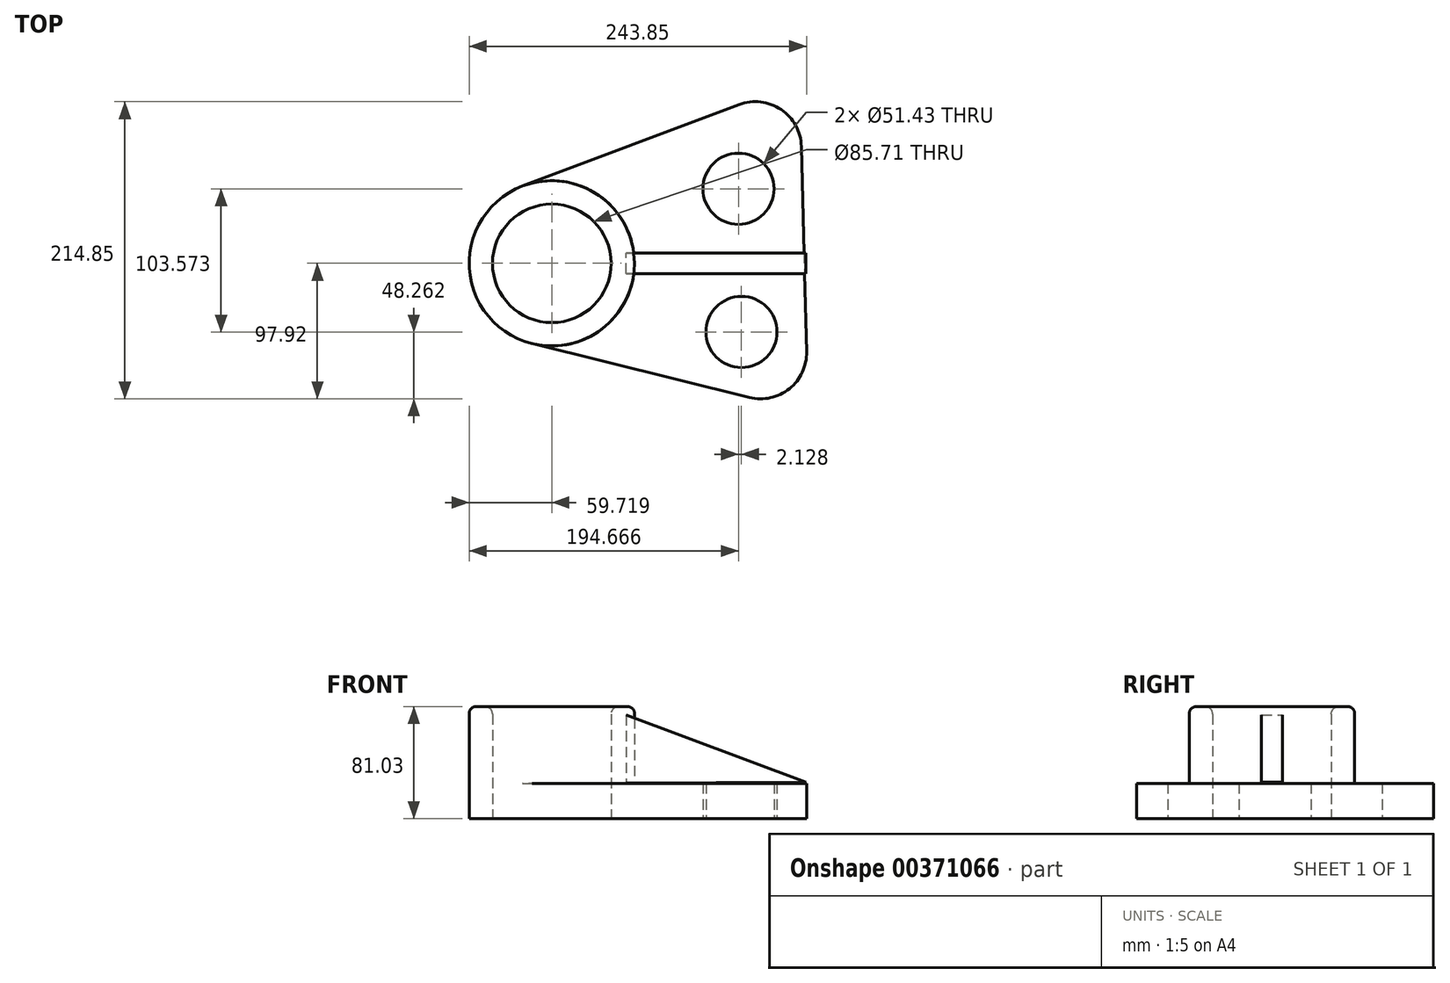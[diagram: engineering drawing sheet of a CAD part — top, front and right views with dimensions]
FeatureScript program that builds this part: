
annotation { "Feature Type Name" : "Feature", "Feature Type Description" : "" }
export const myFeature = defineFeature(function(context is Context, id is Id, definition is map)
    precondition{}
    {
        {
            var Q0;
            Q0=qCreatedBy(makeId("Top.planeOp"),FACE);
            var sketch = newSketch(context, id + "F0", { "sketchPlane" : qUnion([Q0])});
            skCircle(sketch, "E0", {"center": v(-65.07, 0) * mm, "radius": 59.72 * mm});
            skLineSegment(sketch, "E1", {"start": v(-79.44, -57.97) * mm, "end": v(120.16, -107.43) * mm});
            skLineSegment(sketch, "E2", {"start": v(-86.11, 55.9) * mm, "end": v(114.07, 131.26) * mm});
            skLineSegment(sketch, "E3", {"start": v(114.07, 131.26) * mm, "end": v(120.16, -107.43) * mm});
            skCircle(sketch, "E4", {"center": v(-65.07, 0) * mm, "radius": 42.86 * mm});
            skSolve(sketch);
        }
        {
            var Q0;
            Q0=qSketchRegion(id+"F0",true);
            extrude(context, id + "F1", {"entities" : qUnion([Q0]), "depth" : 25.4 * mm});
        }
        {
            var Q0;
            Q0=makeQuery(id+"F0.imprint","IMPRINT",FACE,{"disambiguationData":[TD([[makeQuery(id+"F0.imprint","IMPRINT",EDGE,{"derivedFrom":sQuery(id+"F0.wireOp",EDGE,"E4")}),-1.0]])]});
            extrude(context, id + "F2", {"entities" : qUnion([Q0]), "operationType" : NewBodyOperationType.ADD, "depth" : 81.03 * mm});
        }
        {
            var Q0;
            Q0=makeQuery(id+"F1.opExtrude","SWEPT_EDGE",EDGE,{"disambiguationData":[OSD([sQuery(id+"F0.wireOp",EDGE,"E1"),sQuery(id+"F0.wireOp",EDGE,"E3")])]});
            var Q1;
            Q1=makeQuery(id+"F1.opExtrude","SWEPT_EDGE",EDGE,{"disambiguationData":[OSD([sQuery(id+"F0.wireOp",EDGE,"E2"),sQuery(id+"F0.wireOp",EDGE,"E3")])]});
            fillet(context, id + "F3", {"entities" : qUnion([Q0, Q1]), "radius" : 33.22 * mm, "tangentPropagation" : true, "allowEdgeOverflow" : false});
        }
        {
            var Q0;
            Q0=makeQuery(id+"F2.opExtrude","CAP_EDGE",EDGE,{"disambiguationData":[OSD([sQuery(id+"F0.wireOp",EDGE,"E4")])],"isStart":false});
            fillet(context, id + "F4", {"entities" : qUnion([Q0]), "radius" : 5.52 * mm, "tangentPropagation" : true, "allowEdgeOverflow" : false});
        }
        {
            var Q0;
            Q0=makeQuery(id+"F2.opExtrude","CAP_EDGE",EDGE,{"disambiguationData":[OSD([sQuery(id+"F0.wireOp",EDGE,"E0")])],"isStart":false});
            fillet(context, id + "F5", {"entities" : qUnion([Q0]), "radius" : 5.08 * mm, "tangentPropagation" : true, "allowEdgeOverflow" : false});
        }
        {
            var Q0;
            Q0=qCreatedBy(makeId("Top.planeOp"),FACE);
            var sketch = newSketch(context, id + "F6", { "sketchPlane" : qUnion([Q0])});
            skCircle(sketch, "E5", {"center": v(72, -49.66) * mm, "radius": 25.72 * mm});
            skCircle(sketch, "E6", {"center": v(69.88, 53.91) * mm, "radius": 25.72 * mm});
            skSolve(sketch);
        }
        {
            var Q0;
            Q0=makeQuery(id+"F6.imprint","IMPRINT",FACE,{"disambiguationData":[TD([[makeQuery(id+"F6.imprint","IMPRINT",EDGE,{"derivedFrom":sQuery(id+"F6.wireOp",EDGE,"E5")}),1.0]])]});
            var Q1;
            Q1=makeQuery(id+"F6.imprint","IMPRINT",FACE,{"disambiguationData":[TD([[makeQuery(id+"F6.imprint","IMPRINT",EDGE,{"derivedFrom":sQuery(id+"F6.wireOp",EDGE,"E6")}),1.0]])]});
            var Q2;
            Q2=sQuery(id+"F6.wireOp",EDGE,"E6");
            var Q3;
            Q3=sQuery(id+"F6.wireOp",EDGE,"E5");
            extrude(context, id + "F7", {"entities" : qUnion([Q0, Q1]), "operationType" : NewBodyOperationType.REMOVE, "surfaceEntities" : qUnion([Q2, Q3]), "depth" : 59.18 * mm});
        }
        {
            var Q0;
            Q0=qCreatedBy(makeId("Front.planeOp"),FACE);
            var sketch = newSketch(context, id + "F8", { "sketchPlane" : qUnion([Q0])});
            skLineSegment(sketch, "E7", {"start": v(118.47, 26.38) * mm, "end": v(-11.31, 74.85) * mm});
            skLineSegment(sketch, "E8", {"start": v(-11.31, 74.85) * mm, "end": v(-11.31, 25.74) * mm});
            skLineSegment(sketch, "E9", {"start": v(-11.31, 25.74) * mm, "end": v(118.47, 26.38) * mm});
            skSolve(sketch);
        }
        {
            var Q0;
            Q0=qSketchRegion(id+"F8",true);
            extrude(context, id + "F9", {"entities" : qUnion([Q0]), "endBound" : BoundingType.SYMMETRIC, "depth" : 15 * mm});
        }
    });
